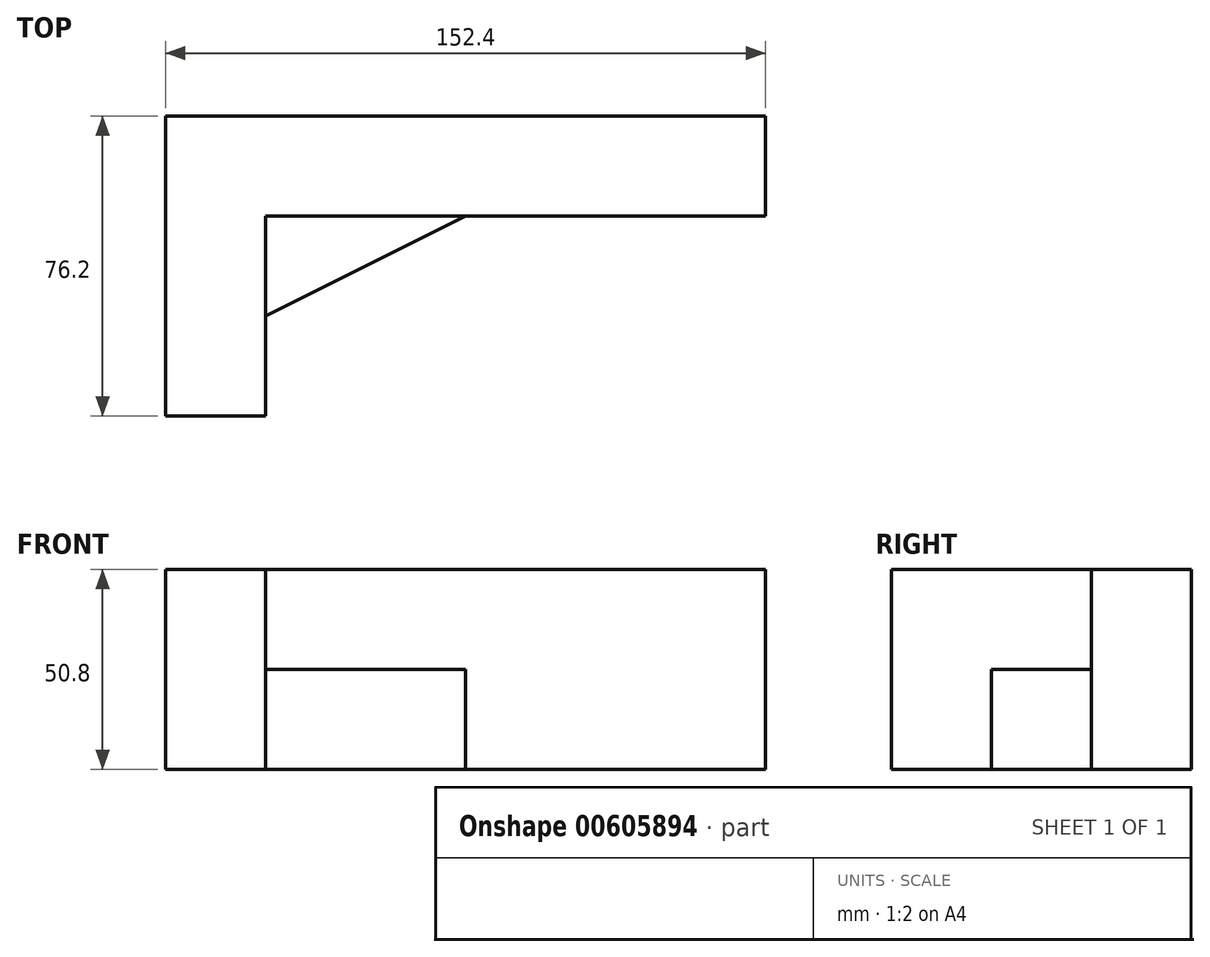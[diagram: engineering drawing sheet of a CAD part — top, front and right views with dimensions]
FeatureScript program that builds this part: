
annotation { "Feature Type Name" : "Feature", "Feature Type Description" : "" }
export const myFeature = defineFeature(function(context is Context, id is Id, definition is map)
    precondition{}
    {
        {
            var Q0;
            Q0=qCreatedBy(makeId("Top.planeOp"),FACE);
            var sketch = newSketch(context, id + "F0", { "sketchPlane" : qUnion([Q0])});
            skLineSegment(sketch, "E0", {"start": v(0, 0) * mm, "end": v(0, 76.2) * mm});
            skLineSegment(sketch, "E1", {"start": v(0, 76.2) * mm, "end": v(152.4, 76.2) * mm});
            skLineSegment(sketch, "E2", {"start": v(152.4, 76.2) * mm, "end": v(152.4, 50.8) * mm});
            skLineSegment(sketch, "E3", {"start": v(25.4, 50.8) * mm, "end": v(25.4, 0) * mm});
            skLineSegment(sketch, "E4", {"start": v(25.4, 0) * mm, "end": v(0, 0) * mm});
            skLineSegment(sketch, "E5", {"start": v(25.4, 50.8) * mm, "end": v(152.4, 50.8) * mm});
            skLineSegment(sketch, "E6", {"start": v(25.4, 0) * mm, "end": v(25.4, 25.4) * mm});
            skLineSegment(sketch, "E7", {"start": v(152.4, 50.8) * mm, "end": v(76.2, 50.8) * mm});
            skLineSegment(sketch, "E8", {"start": v(25.4, 25.4) * mm, "end": v(76.2, 50.8) * mm});
            skSolve(sketch);
        }
        {
            var Q0;
            Q0=makeQuery(id+"F0.imprint","IMPRINT",FACE,{"disambiguationData":[TD([[makeQuery(id+"F0.imprint","IMPRINT",EDGE,{"derivedFrom":sQuery(id+"F0.wireOp",EDGE,"E0")}),-1.0]])]});
            var Q1;
            Q1=makeQuery(id+"F0.imprint","IMPRINT",FACE,{"disambiguationData":[TD([[makeQuery(id+"F0.imprint","IMPRINT",EDGE,{"derivedFrom":sQuery(id+"F0.wireOp",EDGE,"E3")}),1.0]])]});
            extrude(context, id + "F1", {"entities" : qUnion([Q0, Q1]), "depth" : 50.8 * mm, "offsetDistance" : 25.4 * mm});
        }
        {
            var Q0;
            Q0=makeQuery(id+"F1.opExtrude","CAP_FACE",FACE,{"disambiguationData":[OSD([sQuery(id+"F0.wireOp",EDGE,"E0"),sQuery(id+"F0.wireOp",EDGE,"E1"),sQuery(id+"F0.wireOp",EDGE,"E2"),sQuery(id+"F0.wireOp",EDGE,"E4"),sQuery(id+"F0.wireOp",EDGE,"E6"),sQuery(id+"F0.wireOp",EDGE,"E7"),sQuery(id+"F0.wireOp",EDGE,"E8")])],"isStart":false});
            var sketch = newSketch(context, id + "F2", { "sketchPlane" : qUnion([Q0])});
            skLineSegment(sketch, "E9", {"start": v(25.4, 25.4) * mm, "end": v(25.4, 50.8) * mm});
            skLineSegment(sketch, "E10", {"start": v(25.4, 50.8) * mm, "end": v(76.2, 50.8) * mm});
            skSolve(sketch);
        }
        {
            var Q0;
            Q0=makeQuery(id+"F2.imprint","IMPRINT",FACE,{"disambiguationData":[TD([[makeQuery(id+"F2.imprint","IMPRINT",EDGE,{"derivedFrom":sQuery(id+"F2.wireOp",EDGE,"E9")}),-1.0]])]});
            extrude(context, id + "F3", {"entities" : qUnion([Q0]), "operationType" : NewBodyOperationType.REMOVE, "oppositeDirection" : true, "depth" : 25.4 * mm, "offsetDistance" : 25.4 * mm});
        }
    });
